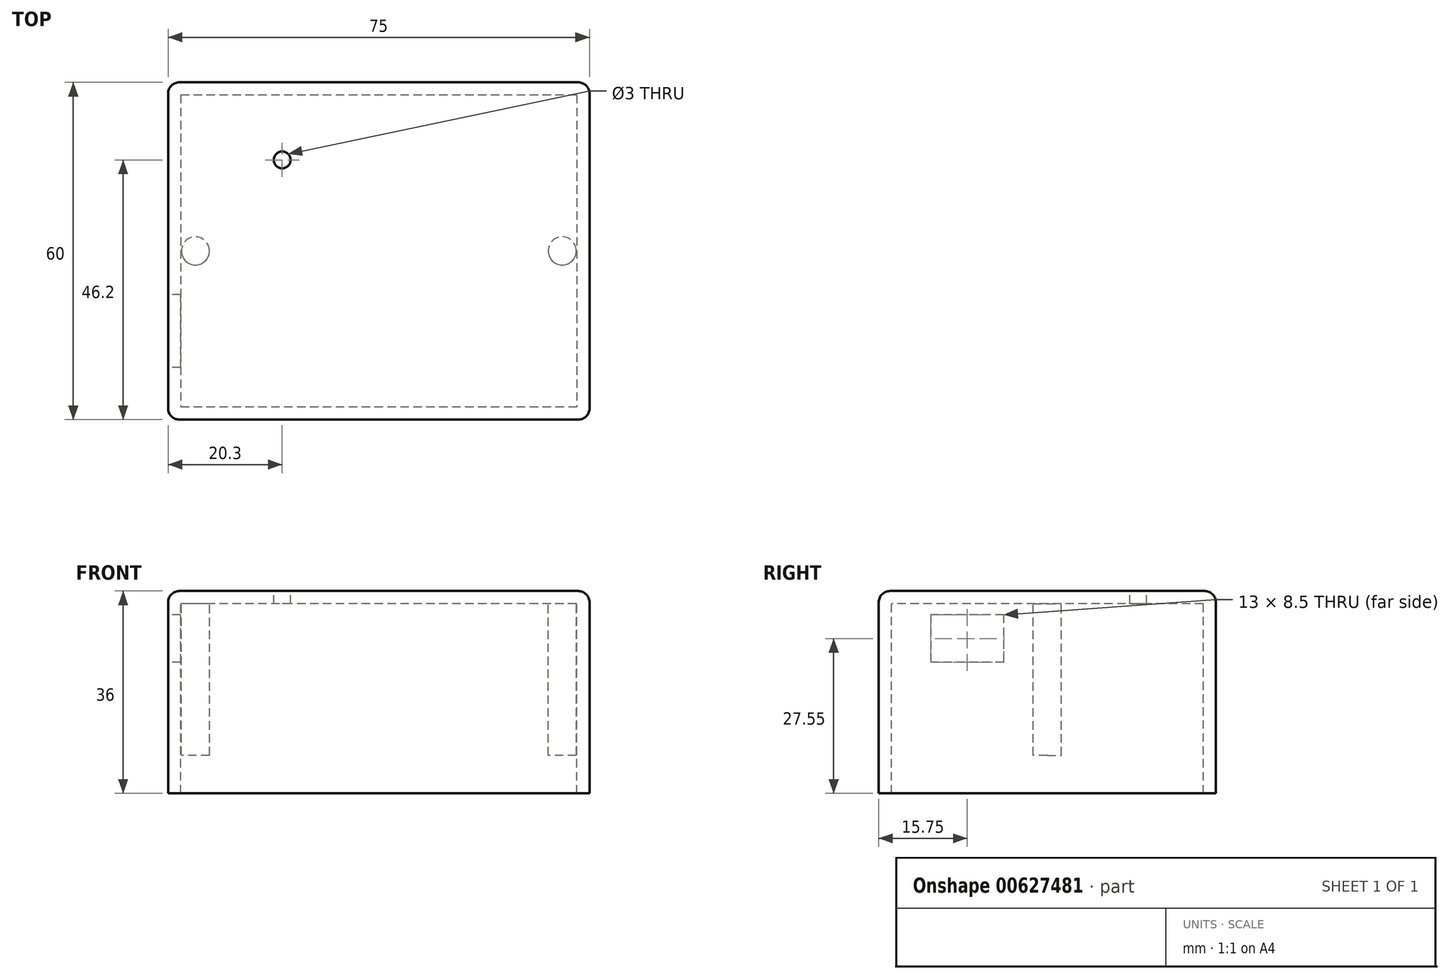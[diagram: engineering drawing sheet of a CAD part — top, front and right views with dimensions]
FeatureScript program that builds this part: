
annotation { "Feature Type Name" : "Feature", "Feature Type Description" : "" }
export const myFeature = defineFeature(function(context is Context, id is Id, definition is map)
    precondition{}
    {
        {
            var Q0;
            Q0=qCreatedBy(makeId("Top.planeOp"),FACE);
            var sketch = newSketch(context, id + "F0", { "sketchPlane" : qUnion([Q0])});
            skLineSegment(sketch, "E0.bottom", {"start": v(37.5, 30) * mm, "end": v(-37.5, 30) * mm});
            skLineSegment(sketch, "E0.top", {"start": v(37.5, -30) * mm, "end": v(-37.5, -30) * mm});
            skLineSegment(sketch, "E0.left", {"start": v(37.5, 30) * mm, "end": v(37.5, -30) * mm});
            skLineSegment(sketch, "E0.right", {"start": v(-37.5, 30) * mm, "end": v(-37.5, -30) * mm});
            skPoint(sketch, "E0.middle", {"position": v(0, 0) * mm});
            skSolve(sketch);
        }
        {
            var Q0;
            Q0 = qSketchRegion(id + "F0", true);
            extrude(context, id + "F1", {"entities" : qUnion([Q0]), "depth" : 36 * mm, "offsetDistance" : 25 * mm});
        }
        {
            var Q0;
            Q0=makeQuery(id+"F1.opExtrude","SWEPT_EDGE",EDGE,{"disambiguationData":[OSD([sQuery(id+"F0.wireOp",EDGE,"E0.bottom"),sQuery(id+"F0.wireOp",EDGE,"E0.right")])]});
            fillet(context, id + "F2", {"entities" : qUnion([Q0]), "radius" : 2 * mm, "tangentPropagation" : true, "allowEdgeOverflow" : false});
        }
        {
            var Q0;
            Q0=makeQuery(id+"F1.opExtrude","SWEPT_EDGE",EDGE,{"disambiguationData":[OSD([sQuery(id+"F0.wireOp",EDGE,"E0.bottom"),sQuery(id+"F0.wireOp",EDGE,"E0.left")])]});
            fillet(context, id + "F3", {"entities" : qUnion([Q0]), "radius" : 2 * mm, "tangentPropagation" : true, "allowEdgeOverflow" : false});
        }
        {
            var Q0;
            Q0=makeQuery(id+"F1.opExtrude","SWEPT_EDGE",EDGE,{"disambiguationData":[OSD([sQuery(id+"F0.wireOp",EDGE,"E0.top"),sQuery(id+"F0.wireOp",EDGE,"E0.left")])]});
            fillet(context, id + "F4", {"entities" : qUnion([Q0]), "radius" : 2 * mm, "tangentPropagation" : true, "allowEdgeOverflow" : false});
        }
        {
            var Q0;
            Q0=makeQuery(id+"F1.opExtrude","SWEPT_EDGE",EDGE,{"disambiguationData":[OSD([sQuery(id+"F0.wireOp",EDGE,"E0.top"),sQuery(id+"F0.wireOp",EDGE,"E0.right")])]});
            fillet(context, id + "F5", {"entities" : qUnion([Q0]), "radius" : 2 * mm, "tangentPropagation" : true, "allowEdgeOverflow" : false});
        }
        {
            var Q0;
            Q0=makeQuery(id+"F1.opExtrude","CAP_EDGE",EDGE,{"disambiguationData":[OSD([sQuery(id+"F0.wireOp",EDGE,"E0.left")])],"isStart":false});
            var Q1;
            Q1=makeQuery(id+"F1.opExtrude","CAP_EDGE",EDGE,{"disambiguationData":[OSD([sQuery(id+"F0.wireOp",EDGE,"E0.top")])],"isStart":false});
            var Q2;
            Q2=makeQuery(id+"F1.opExtrude","CAP_EDGE",EDGE,{"disambiguationData":[OSD([sQuery(id+"F0.wireOp",EDGE,"E0.right")])],"isStart":false});
            var Q3;
            Q3=makeQuery(id+"F1.opExtrude","CAP_FACE",FACE,{"disambiguationData":[OSD([sQuery(id+"F0.wireOp",EDGE,"E0.bottom"),sQuery(id+"F0.wireOp",EDGE,"E0.top"),sQuery(id+"F0.wireOp",EDGE,"E0.left"),sQuery(id+"F0.wireOp",EDGE,"E0.right")])],"isStart":false});
            fillet(context, id + "F6", {"entities" : qUnion([Q0, Q1, Q2, Q3]), "radius" : 2 * mm, "tangentPropagation" : true, "allowEdgeOverflow" : false});
        }
        {
            var Q0;
            Q0=makeQuery(id+"F1.opExtrude","CAP_FACE",FACE,{"disambiguationData":[OSD([sQuery(id+"F0.wireOp",EDGE,"E0.bottom"),sQuery(id+"F0.wireOp",EDGE,"E0.top"),sQuery(id+"F0.wireOp",EDGE,"E0.left"),sQuery(id+"F0.wireOp",EDGE,"E0.right")])],"isStart":true});
            shell(context, id + "F7", {"entities" : qUnion([Q0]), "thickness" : 2.25 * mm});
        }
        {
            var Q0;
            Q0=makeQuery(id+"F7.opShell","OFFSET_FACE",FACE,{"disambiguationData":[OSD([sQuery(id+"F0.wireOp",EDGE,"E0.bottom"),sQuery(id+"F0.wireOp",EDGE,"E0.top"),sQuery(id+"F0.wireOp",EDGE,"E0.left"),sQuery(id+"F0.wireOp",EDGE,"E0.right")])]});
            var sketch = newSketch(context, id + "F8", { "sketchPlane" : qUnion([Q0])});
            skCircle(sketch, "E1", {"center": v(-32.64, 0) * mm, "radius": 2.5 * mm});
            skCircle(sketch, "E2", {"center": v(32.64, 0) * mm, "radius": 2.5 * mm});
            skSolve(sketch);
        }
        {
            var Q0;
            Q0 = qSketchRegion(id + "F8", true);
            extrude(context, id + "F9", {"entities" : qUnion([Q0]), "operationType" : NewBodyOperationType.ADD, "depth" : 27 * mm, "offsetDistance" : 25 * mm});
        }
        {
            var Q0;
            Q0=makeQuery(id+"F1.opExtrude","SWEPT_FACE",FACE,{"disambiguationData":[OSD([sQuery(id+"F0.wireOp",EDGE,"E0.right")])]});
            var sketch = newSketch(context, id + "F10", { "sketchPlane" : qUnion([Q0])});
            skLineSegment(sketch, "E3.bottom", {"start": v(7.75, 31.8) * mm, "end": v(20.75, 31.8) * mm});
            skLineSegment(sketch, "E3.top", {"start": v(7.75, 23.3) * mm, "end": v(20.75, 23.3) * mm});
            skLineSegment(sketch, "E3.left", {"start": v(7.75, 31.8) * mm, "end": v(7.75, 23.3) * mm});
            skLineSegment(sketch, "E3.right", {"start": v(20.75, 31.8) * mm, "end": v(20.75, 23.3) * mm});
            skSolve(sketch);
        }
        {
            var Q0;
            Q0 = qSketchRegion(id + "F10", true);
            extrude(context, id + "F11", {"entities" : qUnion([Q0]), "operationType" : NewBodyOperationType.REMOVE, "oppositeDirection" : true, "depth" : 25 * mm, "offsetDistance" : 25 * mm});
        }
        {
            var Q0;
            Q0=makeQuery(id+"F1.opExtrude","CAP_FACE",FACE,{"disambiguationData":[OSD([sQuery(id+"F0.wireOp",EDGE,"E0.bottom"),sQuery(id+"F0.wireOp",EDGE,"E0.top"),sQuery(id+"F0.wireOp",EDGE,"E0.left"),sQuery(id+"F0.wireOp",EDGE,"E0.right")])],"isStart":false});
            var sketch = newSketch(context, id + "F12", { "sketchPlane" : qUnion([Q0])});
            skCircle(sketch, "E4", {"center": v(-17.2, 16.2) * mm, "radius": 1.5 * mm});
            skSolve(sketch);
        }
        {
            var Q0;
            Q0 = qSketchRegion(id + "F12", true);
            extrude(context, id + "F13", {"entities" : qUnion([Q0]), "operationType" : NewBodyOperationType.REMOVE, "oppositeDirection" : true, "depth" : 25 * mm, "offsetDistance" : 25 * mm});
        }
    });
